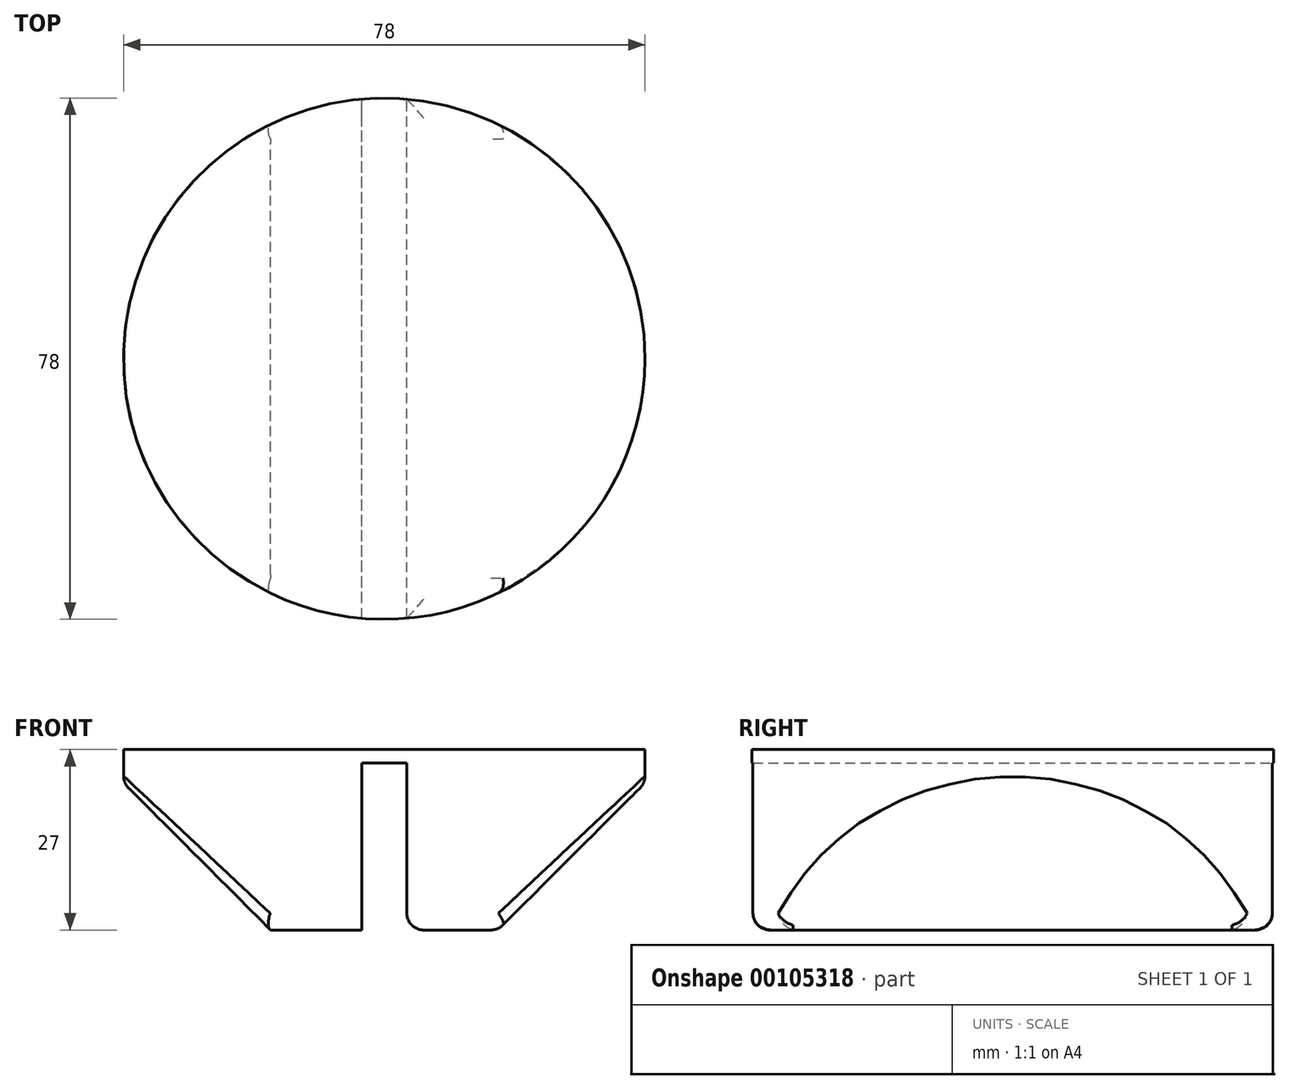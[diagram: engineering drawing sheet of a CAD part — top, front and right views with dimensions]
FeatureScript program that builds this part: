
annotation { "Feature Type Name" : "Feature", "Feature Type Description" : "" }
export const myFeature = defineFeature(function(context is Context, id is Id, definition is map)
    precondition{}
    {
        {
            var Q0;
            Q0=qCreatedBy(makeId("Top.planeOp"),FACE);
            var sketch = newSketch(context, id + "F0", { "sketchPlane" : qUnion([Q0])});
            skCircle(sketch, "E0", {"center": v(0, 0) * mm, "radius": 39 * mm});
            skSolve(sketch);
        }
        {
            var Q0;
            Q0=makeQuery(id+"F0.imprint","IMPRINT",FACE,{"disambiguationData":[TD([[makeQuery(id+"F0.imprint","IMPRINT",EDGE,{"derivedFrom":sQuery(id+"F0.wireOp",EDGE,"E0")}),1.0]])]});
            extrude(context, id + "F1", {"entities" : qUnion([Q0]), "depth" : 27 * mm});
        }
        {
            var Q0;
            Q0=qCreatedBy(makeId("Front.planeOp"),FACE);
            var sketch = newSketch(context, id + "F2", { "sketchPlane" : qUnion([Q0])});
            skLineSegment(sketch, "E1.bottom", {"start": v(-3.38, 0) * mm, "end": v(3.38, 0) * mm});
            skLineSegment(sketch, "E1.top", {"start": v(-3.38, 25) * mm, "end": v(3.37, 25) * mm});
            skLineSegment(sketch, "E1.left", {"start": v(-3.38, 0) * mm, "end": v(-3.38, 25) * mm});
            skLineSegment(sketch, "E1.right", {"start": v(3.38, 0) * mm, "end": v(3.37, 25) * mm});
            skPoint(sketch, "E2", {"position": v(0, 0) * mm});
            skLineSegment(sketch, "E3", {"start": v(17, 0) * mm, "end": v(39, 22) * mm});
            skLineSegment(sketch, "E4", {"start": v(39, 22) * mm, "end": v(39, 0) * mm});
            skLineSegment(sketch, "E5", {"start": v(39, 0) * mm, "end": v(17, 0) * mm});
            skLineSegment(sketch, "E6", {"start": v(0, -6.15) * mm, "end": v(0, 34.82) * mm, "construction": true});
            skLineSegment(sketch, "E7.MirrorCS", {"start": v(-17, 0) * mm, "end": v(-39, 22) * mm});
            skLineSegment(sketch, "E8.MirrorCS", {"start": v(-39, 0) * mm, "end": v(-17, 0) * mm});
            skLineSegment(sketch, "E9.MirrorCS", {"start": v(-39, 22) * mm, "end": v(-39, 0) * mm});
            skSolve(sketch);
        }
        {
            var Q0;
            Q0=makeQuery(id+"F2.imprint","IMPRINT",FACE,{"disambiguationData":[TD([[makeQuery(id+"F2.imprint","IMPRINT",EDGE,{"derivedFrom":sQuery(id+"F2.wireOp",EDGE,"E1.bottom")}),1.0]])]});
            var Q1;
            Q1=makeQuery(id+"F2.imprint","IMPRINT",FACE,{"disambiguationData":[TD([[makeQuery(id+"F2.imprint","IMPRINT",EDGE,{"derivedFrom":sQuery(id+"F2.wireOp",EDGE,"E3")}),-1.0]])]});
            var Q2;
            Q2=makeQuery(id+"F2.imprint","IMPRINT",FACE,{"disambiguationData":[TD([[makeQuery(id+"F2.imprint","IMPRINT",EDGE,{"derivedFrom":sQuery(id+"F2.wireOp",EDGE,"E7.MirrorCS")}),1.0]])]});
            extrude(context, id + "F3", {"entities" : qUnion([Q0, Q1, Q2]), "operationType" : NewBodyOperationType.REMOVE, "endBound" : BoundingType.THROUGH_ALL, "depth" : 25 * mm, "hasSecondDirection" : true, "secondDirectionBound" : SecondDirectionBoundingType.THROUGH_ALL, "secondDirectionOppositeDirection" : true, "secondDirectionDepth" : 25 * mm});
        }
        {
            var Q0;
            Q0=makeQuery(id+"F3.boolean.opBoolean","INTERSECT",EDGE,{"derivedFrom":[makeQuery(id+"F1.opExtrude","SWEPT_FACE",FACE,{"disambiguationData":[OSD([sQuery(id+"F0.wireOp",EDGE,"E0")])]}),makeQuery(id+"F3.opExtrude","SWEPT_FACE",FACE,{"disambiguationData":[OSD([sQuery(id+"F2.wireOp",EDGE,"E3")])]})]});
            var Q1;
            Q1=makeQuery(id+"F3.boolean.opBoolean","INTERSECT",EDGE,{"derivedFrom":[makeQuery(id+"F1.opExtrude","SWEPT_FACE",FACE,{"disambiguationData":[OSD([sQuery(id+"F0.wireOp",EDGE,"E0")])]}),makeQuery(id+"F3.opExtrude","SWEPT_FACE",FACE,{"disambiguationData":[OSD([sQuery(id+"F2.wireOp",EDGE,"E7.MirrorCS")])]})]});
            var Q2;
            Q2=makeQuery(id+"F3.boolean.opBoolean","COPY",EDGE,{"derivedFrom":makeQuery(id+"F3.opExtrude","SWEPT_EDGE",EDGE,{"disambiguationData":[OSD([sQuery(id+"F2.wireOp",EDGE,"E7.MirrorCS"),sQuery(id+"F2.wireOp",EDGE,"E8.MirrorCS")])]})});
            var Q3;
            Q3=makeQuery(id+"F3.boolean.opBoolean","COPY",EDGE,{"derivedFrom":makeQuery(id+"F3.opExtrude","SWEPT_EDGE",EDGE,{"disambiguationData":[OSD([sQuery(id+"F2.wireOp",EDGE,"E3"),sQuery(id+"F2.wireOp",EDGE,"E5")])]})});
            var Q4;
            {var subQ0=sQuery(id+"F0.wireOp",EDGE,"E0");Q4=makeQuery(id+"F3.boolean.opBoolean","SPLIT",EDGE,{"disambiguationData":[TD([makeQuery(id+"F1.opExtrude","SWEPT_FACE",FACE,{"disambiguationData":[OSD([subQ0])]}),makeQuery(id+"F1.opExtrude","CAP_FACE",FACE,{"disambiguationData":[OSD([subQ0])],"isStart":true}),makeQuery(id+"F3.opExtrude","SWEPT_FACE",FACE,{"disambiguationData":[OSD([sQuery(id+"F2.wireOp",EDGE,"E1.left")])]}),makeQuery(id+"F3.opExtrude","SWEPT_FACE",FACE,{"disambiguationData":[OSD([sQuery(id+"F2.wireOp",EDGE,"E7.MirrorCS")])]})]),OD(0.0)],"derivedFrom":makeQuery(id+"F1.opExtrude","CAP_EDGE",EDGE,{"disambiguationData":[OSD([subQ0])],"isStart":true})});}
            var Q5;
            {var subQ0=sQuery(id+"F0.wireOp",EDGE,"E0");Q5=makeQuery(id+"F3.boolean.opBoolean","SPLIT",EDGE,{"disambiguationData":[TD([makeQuery(id+"F1.opExtrude","SWEPT_FACE",FACE,{"disambiguationData":[OSD([subQ0])]}),makeQuery(id+"F1.opExtrude","CAP_FACE",FACE,{"disambiguationData":[OSD([subQ0])],"isStart":true}),makeQuery(id+"F3.opExtrude","SWEPT_FACE",FACE,{"disambiguationData":[OSD([sQuery(id+"F2.wireOp",EDGE,"E1.right")])]}),makeQuery(id+"F3.opExtrude","SWEPT_FACE",FACE,{"disambiguationData":[OSD([sQuery(id+"F2.wireOp",EDGE,"E3")])]})]),OD(0.0)],"derivedFrom":makeQuery(id+"F1.opExtrude","CAP_EDGE",EDGE,{"disambiguationData":[OSD([subQ0])],"isStart":true})});}
            var Q6;
            {var subQ0=sQuery(id+"F0.wireOp",EDGE,"E0");Q6=makeQuery(id+"F3.boolean.opBoolean","SPLIT",EDGE,{"disambiguationData":[TD([makeQuery(id+"F1.opExtrude","SWEPT_FACE",FACE,{"disambiguationData":[OSD([subQ0])]}),makeQuery(id+"F1.opExtrude","CAP_FACE",FACE,{"disambiguationData":[OSD([subQ0])],"isStart":true}),makeQuery(id+"F3.opExtrude","SWEPT_FACE",FACE,{"disambiguationData":[OSD([sQuery(id+"F2.wireOp",EDGE,"E1.right")])]}),makeQuery(id+"F3.opExtrude","SWEPT_FACE",FACE,{"disambiguationData":[OSD([sQuery(id+"F2.wireOp",EDGE,"E3")])]})]),OD(1.0)],"derivedFrom":makeQuery(id+"F1.opExtrude","CAP_EDGE",EDGE,{"disambiguationData":[OSD([subQ0])],"isStart":true})});}
            var Q7;
            {var subQ0=sQuery(id+"F0.wireOp",EDGE,"E0");Q7=makeQuery(id+"F3.boolean.opBoolean","SPLIT",EDGE,{"disambiguationData":[TD([makeQuery(id+"F1.opExtrude","SWEPT_FACE",FACE,{"disambiguationData":[OSD([subQ0])]}),makeQuery(id+"F1.opExtrude","CAP_FACE",FACE,{"disambiguationData":[OSD([subQ0])],"isStart":true}),makeQuery(id+"F3.opExtrude","SWEPT_FACE",FACE,{"disambiguationData":[OSD([sQuery(id+"F2.wireOp",EDGE,"E1.left")])]}),makeQuery(id+"F3.opExtrude","SWEPT_FACE",FACE,{"disambiguationData":[OSD([sQuery(id+"F2.wireOp",EDGE,"E7.MirrorCS")])]})]),OD(1.0)],"derivedFrom":makeQuery(id+"F1.opExtrude","CAP_EDGE",EDGE,{"disambiguationData":[OSD([subQ0])],"isStart":true})});}
            var Q8;
            Q8=makeQuery(id+"F3.boolean.opBoolean","COPY",EDGE,{"derivedFrom":makeQuery(id+"F3.opExtrude","SWEPT_EDGE",EDGE,{"disambiguationData":[OSD([sQuery(id+"F2.wireOp",EDGE,"E1.bottom"),sQuery(id+"F2.wireOp",EDGE,"E1.right")])]})});
            var Q9;
            Q9=makeQuery(id+"F3.boolean.opBoolean","COPY",EDGE,{"derivedFrom":makeQuery(id+"F3.opExtrude","SWEPT_EDGE",EDGE,{"disambiguationData":[OSD([sQuery(id+"F2.wireOp",EDGE,"E1.bottom"),sQuery(id+"F2.wireOp",EDGE,"E1.left")])]})});
            fillet(context, id + "F4", {"entities" : qUnion([Q0, Q1, Q2, Q3, Q4, Q5, Q6, Q7, Q8, Q9]), "radius" : 2.5 * mm, "tangentPropagation" : true, "allowEdgeOverflow" : false});
        }
    });
